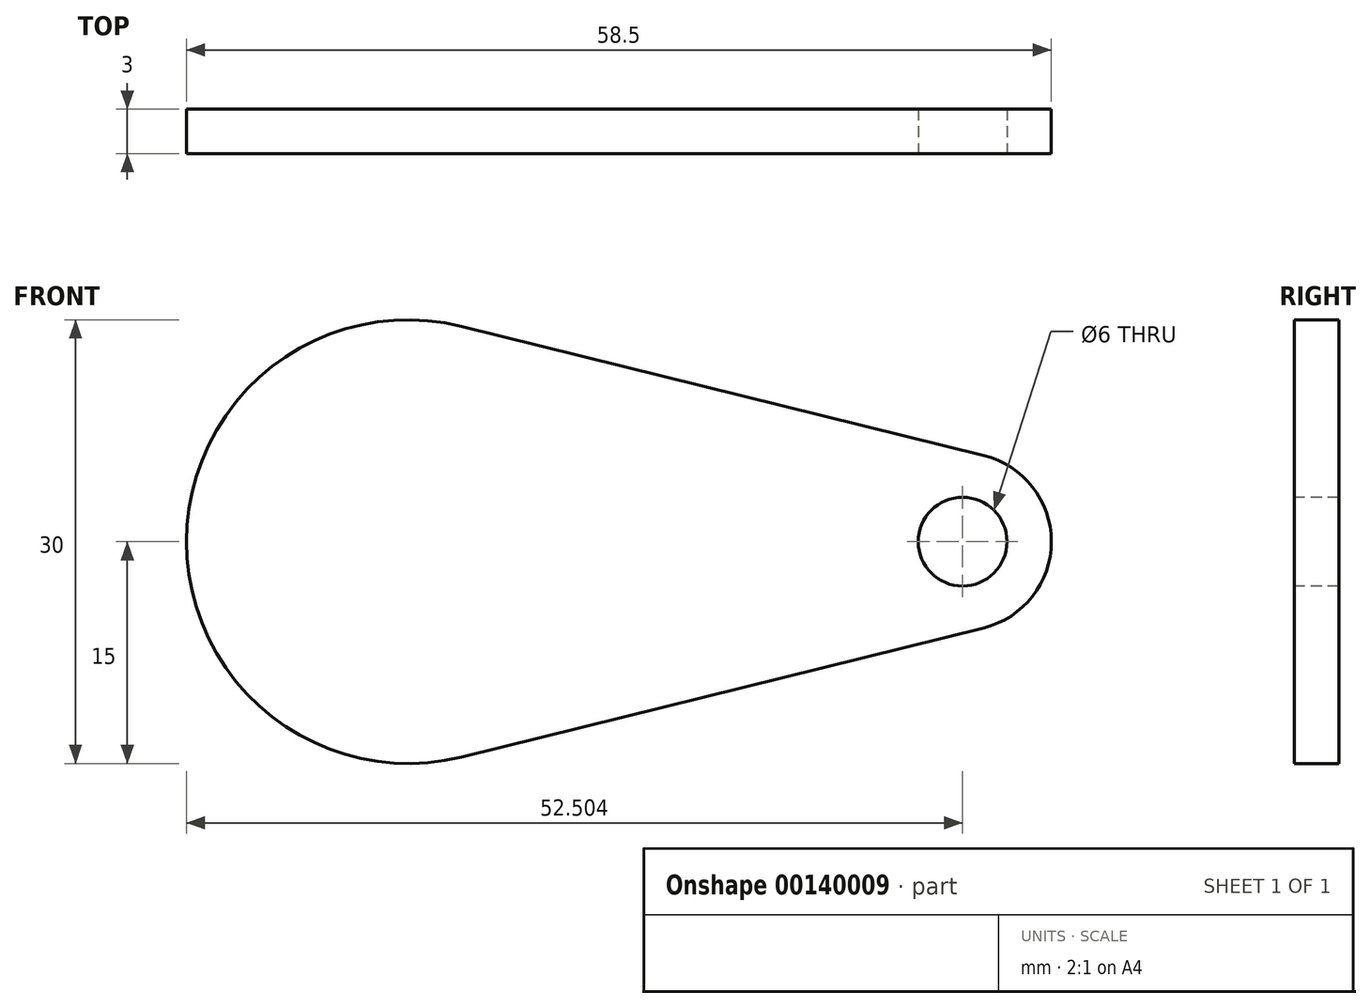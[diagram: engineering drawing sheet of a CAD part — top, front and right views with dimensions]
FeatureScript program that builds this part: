
annotation { "Feature Type Name" : "Feature", "Feature Type Description" : "" }
export const myFeature = defineFeature(function(context is Context, id is Id, definition is map)
    precondition{}
    {
        {
            var Q0;
            Q0=qCreatedBy(makeId("Front.planeOp"),FACE);
            var sketch = newSketch(context, id + "F0", { "sketchPlane" : qUnion([Q0])});
            skCircle(sketch, "E0", {"center": v(-26.07, 0) * mm, "radius": 15 * mm});
            skCircle(sketch, "E1", {"center": v(11.43, 0) * mm, "radius": 6 * mm});
            skLineSegment(sketch, "E2", {"start": v(-22.47, 14.56) * mm, "end": v(12.87, 5.82) * mm});
            skLineSegment(sketch, "E3", {"start": v(-22.47, -14.56) * mm, "end": v(12.87, -5.82) * mm});
            skSolve(sketch);
        }
        {
            var Q0;
            {var subQ0=sQuery(id+"F0.wireOp",EDGE,"E0");var subQ1=makeQuery(id+"F0.imprint","INTERSECT",VERTEX,{"derivedFrom":[subQ0,sQuery(id+"F0.wireOp",EDGE,"E2")]});Q0=makeQuery(id+"F0.imprint","IMPRINT",FACE,{"disambiguationData":[TD([[makeQuery(id+"F0.imprint","IMPRINT",EDGE,{"disambiguationData":[TD([[subQ1,-1.0]])],"derivedFrom":subQ0}),1.0]])]});}
            var Q1;
            {var subQ0=sQuery(id+"F0.wireOp",EDGE,"E2");Q1=makeQuery(id+"F0.imprint","IMPRINT",FACE,{"disambiguationData":[TD([[makeQuery(id+"F0.imprint","IMPRINT",EDGE,{"derivedFrom":subQ0}),-1.0]])]});}
            var Q2;
            {var subQ0=sQuery(id+"F0.wireOp",EDGE,"E1");var subQ1=makeQuery(id+"F0.imprint","INTERSECT",VERTEX,{"derivedFrom":[subQ0,sQuery(id+"F0.wireOp",EDGE,"E2")]});Q2=makeQuery(id+"F0.imprint","IMPRINT",FACE,{"disambiguationData":[TD([[makeQuery(id+"F0.imprint","IMPRINT",EDGE,{"disambiguationData":[TD([[subQ1,-1.0]])],"derivedFrom":subQ0}),1.0]])]});}
            extrude(context, id + "F1", {"entities" : qUnion([Q0, Q1, Q2]), "depth" : 3 * mm});
        }
        {
            var Q0;
            Q0=makeQuery(id+"F1.opExtrude","CAP_FACE",FACE,{"disambiguationData":[OSD([sQuery(id+"F0.wireOp",EDGE,"E0"),sQuery(id+"F0.wireOp",EDGE,"E1"),sQuery(id+"F0.wireOp",EDGE,"E2"),sQuery(id+"F0.wireOp",EDGE,"E3")])],"isStart":false});
            var sketch = newSketch(context, id + "F2", { "sketchPlane" : qUnion([Q0])});
            skCircle(sketch, "E4", {"center": v(11.43, 0) * mm, "radius": 3 * mm});
            skSolve(sketch);
        }
        {
            var Q0;
            Q0=makeQuery(id+"F2.imprint","IMPRINT",FACE,{"disambiguationData":[TD([[makeQuery(id+"F2.imprint","IMPRINT",EDGE,{"derivedFrom":sQuery(id+"F2.wireOp",EDGE,"E4")}),1.0]])]});
            extrude(context, id + "F3", {"entities" : qUnion([Q0]), "operationType" : NewBodyOperationType.REMOVE, "oppositeDirection" : true, "depth" : 25 * mm});
        }
    });
